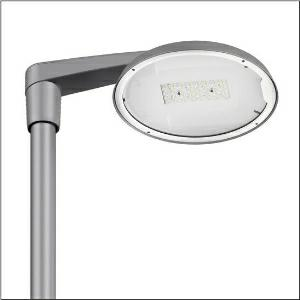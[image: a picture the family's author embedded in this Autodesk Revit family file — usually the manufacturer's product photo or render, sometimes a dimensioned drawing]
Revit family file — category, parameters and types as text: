
# Revit family: dl_50_iq_mini___st0_5a_5xa248b41f08fe_6912
name_source: partatom
category: Lighting Fixtures
units: mm (PartAtom-declared; Revit-internal decimal feet)

## family parameters
Cut with Voids When Loaded = No
Host = Face
Light Source = No
Part Type = Normal
Room Calculation Point = No
Round Connector Dimension = Use Diameter
Shared = No

## types (1)
- --- (1 x LED, 2690 lm, 15.7 W, 4000K)
    Apparent Load = 16 VA
    CIE Flux Codes = 41 75 97 100 100
    Color Rendering = 70
    Color Temperature = 4000K
    Default Elevation = 1800 mm
    Description = DL 50 iQ mini, mast luminaire, primary light control with lens, of PMMA, primary optical cover: cover, of toughened safety glass, transparent, light distribution: ST0.5a, light emission: direct distribution, primary light characteristic: asymmetric, installation type: side-entry, post-top, LED, High Power LED, rated luminous flux: 2.690lm, luminous efficacy: 171lm/W, light colour: 740, colour temperature: 4000K, control gear: iQ Street-Remote, control: optimised constant luminous flux control (CLO 2.0), Desk-Remote (wireless, voltage-free reading and setting of iQ features in the workshop via application-optimized NFC function/RFID function), Light-Fading, Smart-Wire, Night-Set, Lumen-Switch, Temp-Guard, Auto-Match, Street-Remote, mains connection: 230..240V, AC, 50/60Hz, connection cable pre-assembled, cable length: 6,5m, start of lifetime: 16W, end of service life: 16W, reduction: 8W, luminaire housing, of diecast aluminium, powder-coated, SITECO metallic grey (DB 702S), inclination adjustable: 0°, 5°, 10° (post-top) | 0°, -5°, -10°, -15° (side-entry), please order mast post-top element or mast side-entry element separately, diameter: 500mm, height: 115mm, post-top: for spigot size d x l = 76 x 100mm; with reducer (optional accessory) 60 x 100mm | side-entry: for spigot size d x l = 60 x 100mm; with reducer (optional accessory) 42 x 100mm, mounting height: 4..6m, protection rating (complete): IP66, insulation class (complete): insulation class II (safety insulation), certification: CE, ENEC, ENEC+, VDE, impact resistance: IK08, permissible operating ambient temperature for outdoor applications: -25..+40°C, standard-compliant lighting for roads and squares, packaging unit: 1 piece

Light Distribution: ST0.5a
    Height = 115 mm
    Lamp = 1 x LED
    Lamp Light Flux = 2690 lm
    Lamp Power = 15.7 W
    Lamp count = 1
    Length = 500 mm
    Luminous efficacy = 171 lm/W
    Manufacturer = Siteco
    ModVariant = No
    Model = 5XA248B41F08FE
    Number of Poles = 1
    OnlyDefault = Yes
    Power Factor = 1
    Product Name = DL 50 iQ mini | ST0.5a
    Product group = mast luminaire | pylon top
    ProductGroupID = 6100
    Protection Class = Protection class II
    Protection Degree = IP 66
    RLX_Detail_Level = 1
    RLX_Emergency_Light_Flux = 0 lm
    RLX_Emergency_Type = 0
    RLX_Emergency_Type_DB = No
    RlxData = <blob elided: 126877 chars, md5=5c581f67>
    Socket = socket
    Standby Power = 0 W
    System Light Flux = 2690 lm
    System Power = 16 W
    Type Comments = factory setting: luminous flux: 100 % | dim-lin: 254 | 319 mA
    Type Image = l_1251794.jpg
    URL = http://relux.com
    VarID = @adj_138891
    Voltage = 0 V
    Weight = 0.00 kg
    Width = 0 mm  [stored 0 ft]

note: [stored X ft] marks values corroborated as IEEE doubles in the binary element streams (Revit-internal decimal feet)

## geometry (parser evidence)
native form markers: Blend x4, Sweep x12
no freeform markers — native parametric forms only
